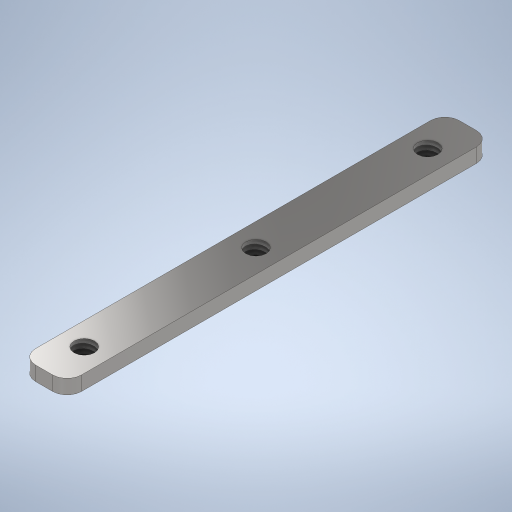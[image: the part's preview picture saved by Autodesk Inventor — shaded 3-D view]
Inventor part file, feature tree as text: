
AUTODESK INVENTOR PART (.ipt)
format: ipt  version: 2023 (Build 270158000, 158)  size: 262,656 bytes
history: native  units: in
note: dims shown in document units (in); Inventor stores cm internally (conversion verified against a paired STEP export)
features: sketch x2, extrude x1, hole x1, fillet x1
ambient origin geometry x8: Origin, YZ Plane, XZ Plane, XY Plane, X Axis, Y Axis, Z Axis, Center Point
bodies: Solid1 (feature_tree)
feature tree (5):
  extrude  "Extrusion1"  Depth=1.85in
  hole  "Hole1"  [1 undecoded]
  fillet  "Fillet1"  Radius=0.75in
  sketch  "Sketch1"  dims[d0=0.2in d1=1.85in]
  sketch  "Sketch2"  dims[d2=0.0625in d3=0.0in d4=0.75in d5=0.75in d6=0.0894in d7=0.224in d8=0.172in d9=0.25in d10=0.5635in d11=1.0in d12=0.8108in d13=0.0625in]
note: 1 required parameter value undecoded (feature->parameter linkage not recoverable at this tier; creation-order binding heuristic only, values carry confidence <= 0.55)
